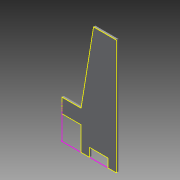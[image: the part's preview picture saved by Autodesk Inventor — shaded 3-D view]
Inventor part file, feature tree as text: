
AUTODESK INVENTOR PART (.ipt)
format: ipt  version: 2013 (Build 170138000, 138)  size: 111,104 bytes
history: native  units: mm
features: sketch x4, extrude x2
ambient origin geometry x8: Origin, YZ Plane, XZ Plane, XY Plane, X Axis, Y Axis, Z Axis, Center Point
bodies: Solid1 (feature_tree)
feature tree (6):
  extrude  "Extrusion1"  Depth=200.0mm
  sketch  "Sketch2"  dims[d6=20.0mm d7=0.0mm d8=370.0mm]
  sketch  "Sketch3"  dims[d9=150.0mm]
  extrude  "Extrusion2"  Depth=370.0mm
  sketch  "Sketch1"  dims[d2=1200.0mm d4=200.0mm]
  sketch  "Sketch4"  dims[d10=250.0mm d11=90.0mm d12=90.0mm d13=190.0mm d14=240.0mm d15=8.0mm d16=10.0mm d17=0.0mm]
